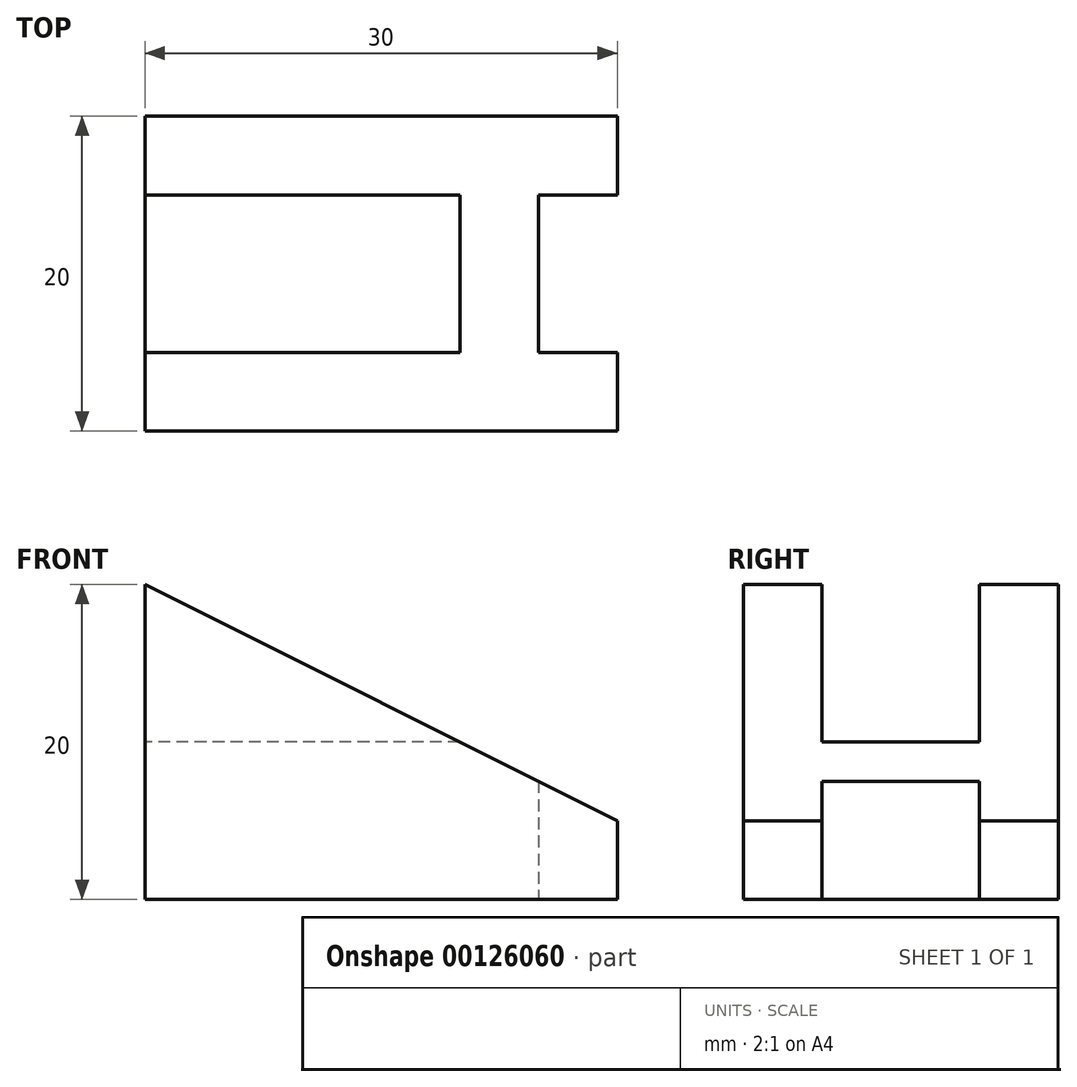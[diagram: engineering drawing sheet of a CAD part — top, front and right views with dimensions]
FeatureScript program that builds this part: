
annotation { "Feature Type Name" : "Feature", "Feature Type Description" : "" }
export const myFeature = defineFeature(function(context is Context, id is Id, definition is map)
    precondition{}
    {
        {
            var Q0;
            Q0=qCreatedBy(makeId("Front.planeOp"),FACE);
            var sketch = newSketch(context, id + "F0", { "sketchPlane" : qUnion([Q0])});
            skLineSegment(sketch, "E0", {"start": v(0, 0) * mm, "end": v(30, 0) * mm});
            skLineSegment(sketch, "E1", {"start": v(0, 0) * mm, "end": v(0, 20) * mm});
            skLineSegment(sketch, "E2", {"start": v(30, 0) * mm, "end": v(30, 5) * mm});
            skLineSegment(sketch, "E3", {"start": v(30, 5) * mm, "end": v(0, 20) * mm});
            skSolve(sketch);
        }
        {
            var Q0;
            Q0 = qSketchRegion(id + "F0", true);
            extrude(context, id + "F1", {"entities" : qUnion([Q0]), "endBound" : BoundingType.SYMMETRIC, "depth" : 20 * mm});
        }
        {
            var Q0;
            Q0=qCreatedBy(makeId("Top.planeOp"),FACE);
            var sketch = newSketch(context, id + "F2", { "sketchPlane" : qUnion([Q0])});
            skLineSegment(sketch, "E4.bottom", {"start": v(30, -5) * mm, "end": v(25, -5) * mm});
            skLineSegment(sketch, "E4.top", {"start": v(30, 5) * mm, "end": v(25, 5) * mm});
            skLineSegment(sketch, "E4.left", {"start": v(30, -5) * mm, "end": v(30, 5) * mm});
            skLineSegment(sketch, "E4.right", {"start": v(25, -5) * mm, "end": v(25, 5) * mm});
            skSolve(sketch);
        }
        {
            var Q0;
            Q0 = qSketchRegion(id + "F2", true);
            extrude(context, id + "F3", {"entities" : qUnion([Q0]), "operationType" : NewBodyOperationType.REMOVE, "depth" : 8 * mm});
        }
        {
            var Q0;
            Q0=qCreatedBy(makeId("Right.planeOp"),FACE);
            var sketch = newSketch(context, id + "F4", { "sketchPlane" : qUnion([Q0])});
            skLineSegment(sketch, "E5.bottom", {"start": v(-5, 20) * mm, "end": v(5, 20) * mm});
            skLineSegment(sketch, "E5.top", {"start": v(-5, 10) * mm, "end": v(5, 10) * mm});
            skLineSegment(sketch, "E5.left", {"start": v(-5, 20) * mm, "end": v(-5, 10) * mm});
            skLineSegment(sketch, "E5.right", {"start": v(5, 20) * mm, "end": v(5, 10) * mm});
            skSolve(sketch);
        }
        {
            var Q0;
            Q0 = qSketchRegion(id + "F4", true);
            extrude(context, id + "F5", {"entities" : qUnion([Q0]), "operationType" : NewBodyOperationType.REMOVE, "depth" : 20 * mm});
        }
    });
